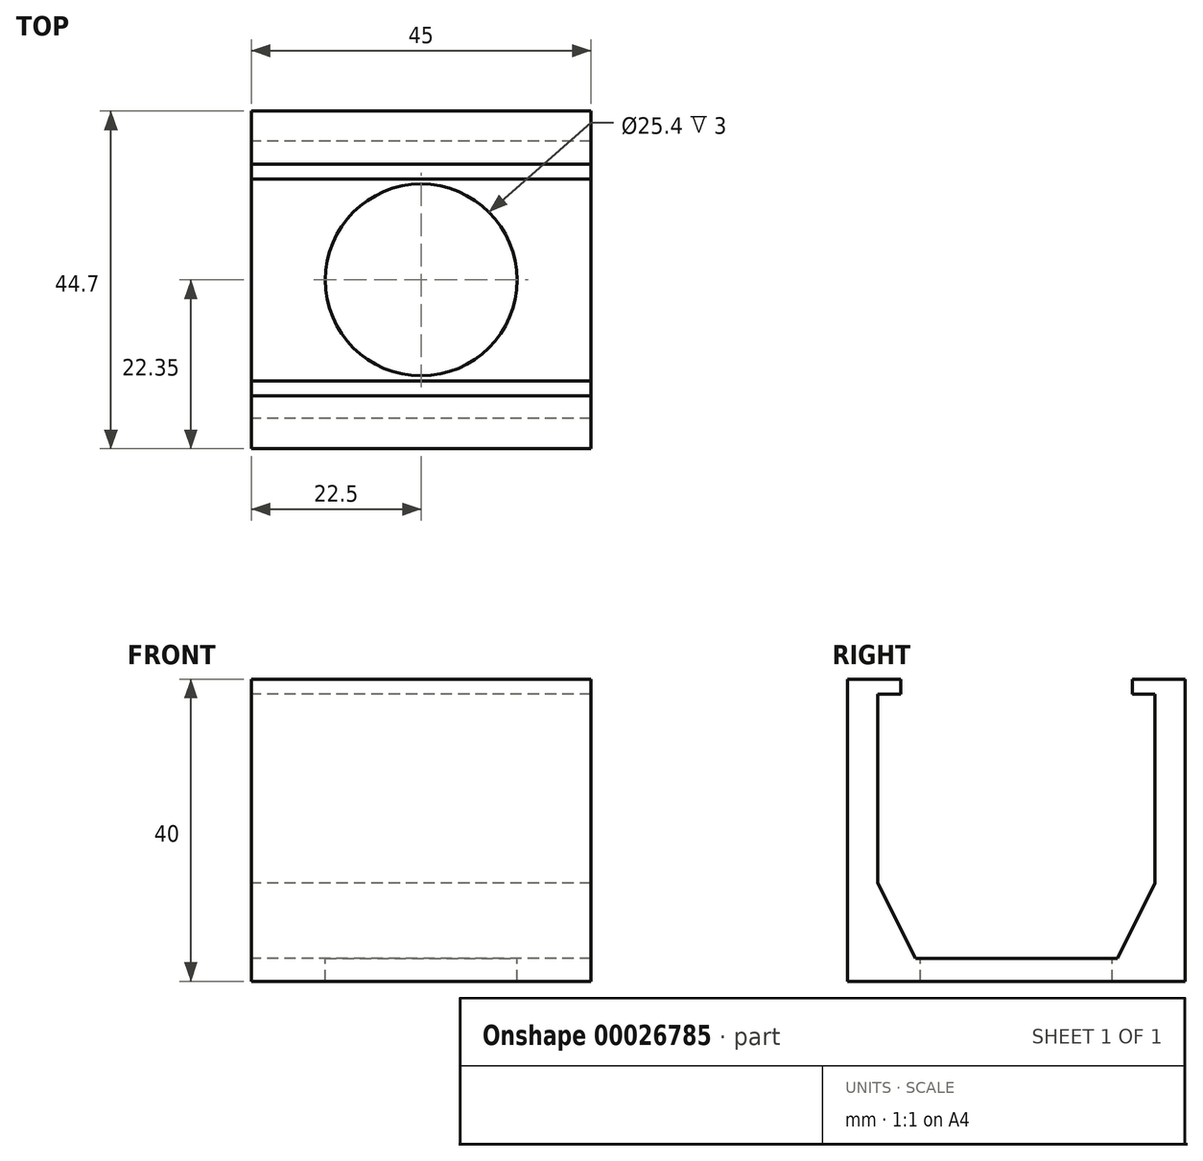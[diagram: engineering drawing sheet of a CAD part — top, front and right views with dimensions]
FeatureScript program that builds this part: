
annotation { "Feature Type Name" : "Feature", "Feature Type Description" : "" }
export const myFeature = defineFeature(function(context is Context, id is Id, definition is map)
    precondition{}
    {
        {
            var Q0;
            Q0=qCreatedBy(makeId("Right.planeOp"),FACE);
            var sketch = newSketch(context, id + "F0", { "sketchPlane" : qUnion([Q0])});
            skLineSegment(sketch, "E0.rect.bottom", {"start": v(22.35, 16) * mm, "end": v(15.35, 16) * mm});
            skLineSegment(sketch, "E0.rect.top", {"start": v(22.35, -24) * mm, "end": v(-22.35, -24) * mm});
            skLineSegment(sketch, "E0.rect.left", {"start": v(22.35, 16) * mm, "end": v(22.35, -24) * mm});
            skLineSegment(sketch, "E0.rect.right", {"start": v(-22.35, 16) * mm, "end": v(-22.35, -24) * mm});
            skPoint(sketch, "E0.rect.middle", {"position": v(0, 0) * mm});
            skLineSegment(sketch, "E1.rect.top", {"start": v(15.35, -21) * mm, "end": v(-15.35, -21) * mm});
            skLineSegment(sketch, "E1.rect.left", {"start": v(15.35, 16) * mm, "end": v(15.35, 14) * mm});
            skLineSegment(sketch, "E1.rect.right", {"start": v(-15.35, 16) * mm, "end": v(-15.35, 14) * mm});
            skPoint(sketch, "E1.rect.middle", {"position": v(0, -2.5) * mm});
            skLineSegment(sketch, "E2.trimOffspring", {"start": v(-15.35, 16) * mm, "end": v(-22.35, 16) * mm});
            skLineSegment(sketch, "E3.bottom", {"start": v(-18.35, 14) * mm, "end": v(-15.35, 14) * mm});
            skLineSegment(sketch, "E3.top", {"start": v(-18.35, -21) * mm, "end": v(18.35, -21) * mm});
            skLineSegment(sketch, "E3.left", {"start": v(-18.35, 14) * mm, "end": v(-18.35, -21) * mm});
            skLineSegment(sketch, "E3.right", {"start": v(18.35, 14) * mm, "end": v(18.35, -21) * mm});
            skLineSegment(sketch, "E4.trimOffspring", {"start": v(15.35, 14) * mm, "end": v(18.35, 14) * mm});
            skLineSegment(sketch, "E5", {"start": v(-18.35, -11) * mm, "end": v(-13.35, -21) * mm});
            skLineSegment(sketch, "E6", {"start": v(13.35, -21) * mm, "end": v(18.35, -11) * mm});
            skSolve(sketch);
        }
        {
            var Q0;
            Q0 = qSketchRegion(id + "F0", true);
            extrude(context, id + "F1", {"entities" : qUnion([Q0]), "endBound" : BoundingType.SYMMETRIC, "depth" : 45 * mm});
        }
        {
            var Q0;
            Q0=qCreatedBy(makeId("Top.planeOp"),FACE);
            var sketch = newSketch(context, id + "F2", { "sketchPlane" : qUnion([Q0])});
            skCircle(sketch, "E7", {"center": v(0, 0) * mm, "radius": 12.7 * mm});
            skSolve(sketch);
        }
        {
            var Q0;
            Q0 = qSketchRegion(id + "F2", true);
            extrude(context, id + "F3", {"entities" : qUnion([Q0]), "operationType" : NewBodyOperationType.REMOVE, "oppositeDirection" : true, "depth" : 25 * mm});
        }
    });
